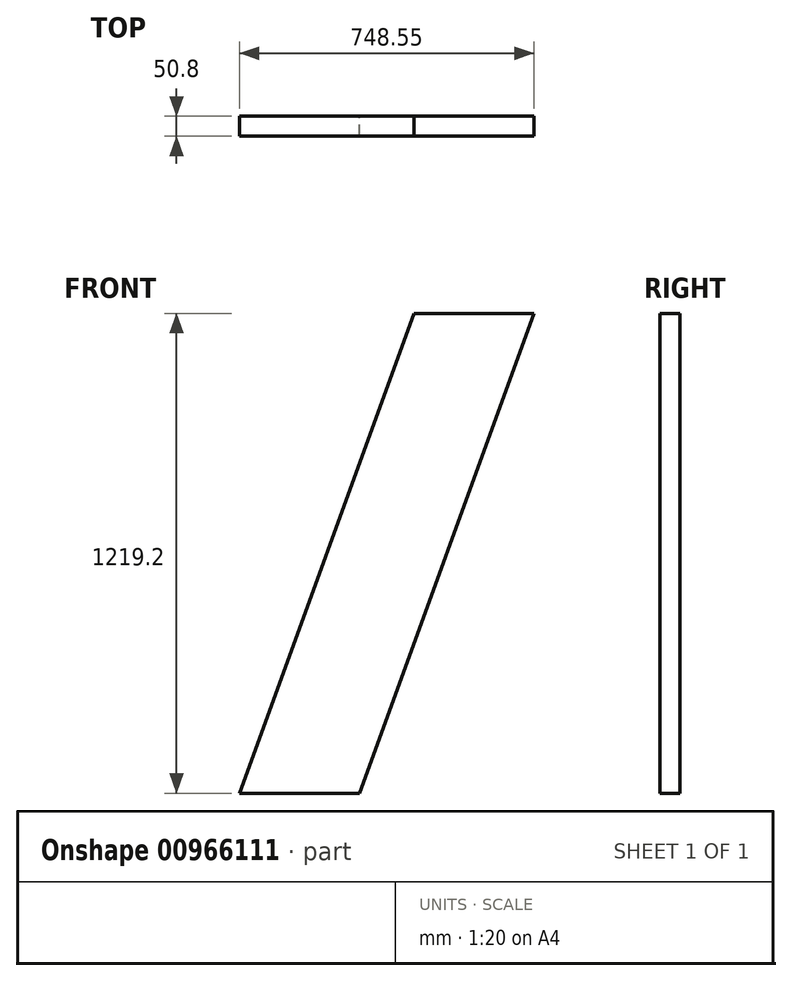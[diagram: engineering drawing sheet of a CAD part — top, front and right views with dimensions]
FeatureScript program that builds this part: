
annotation { "Feature Type Name" : "Feature", "Feature Type Description" : "" }
export const myFeature = defineFeature(function(context is Context, id is Id, definition is map)
    precondition{}
    {
        {
            var Q0;
            Q0=qCreatedBy(makeId("Front.planeOp"),FACE);
            var sketch = newSketch(context, id + "F0", { "sketchPlane" : qUnion([Q0])});
            skLineSegment(sketch, "E0", {"start": v(0, 0) * mm, "end": v(304.8, 0) * mm});
            skLineSegment(sketch, "E1", {"start": v(304.8, 0) * mm, "end": v(748.55, 1219.2) * mm});
            skLineSegment(sketch, "E2", {"start": v(748.55, 1219.2) * mm, "end": v(443.75, 1219.2) * mm});
            skLineSegment(sketch, "E3", {"start": v(443.75, 1219.2) * mm, "end": v(0, 0) * mm});
            skSolve(sketch);
        }
        {
            var Q0;
            Q0=makeQuery(id+"F0.imprint","IMPRINT",FACE,{"disambiguationData":[TD([[makeQuery(id+"F0.imprint","IMPRINT",EDGE,{"derivedFrom":sQuery(id+"F0.wireOp",EDGE,"E0")}),1.0]])]});
            extrude(context, id + "F1", {"entities" : qUnion([Q0]), "depth" : 50.8 * mm, "offsetDistance" : 25.4 * mm});
        }
    });
